# Revit family: QSC TSC80W-G2_R15
name_source: partatom
category: Communication Devices
revit_build: Autodesk Revit 2015 (Build: 20160512_0715(x64)
units: mm (PartAtom-declared; Revit-internal decimal feet)

## types (1)
- QSC TSC80W-G2_R15
    Brightness Full = 400 Nits
    Current Draw = 0.5
    Default Elevation = 0.0 mm
    Depth = 33.7 mm
    Description = In-Wall or Table Top Touch Screen Controller
    Enclosure Material = Steel, Paint Finish, Dark Gray, Matte
    Face Material = Glossy Black
    Heat Load = 17 typical
    Height = 87.5 mm
    Manufacturer = QSC
    Manufacturer URL = http://www.qsc.com
    Model = TSC-55W-G2
    OmniClass Number = 23-19 11 25
    Product Documentation Link = https://www.qsc.com
    Resolution Horizontal = 960
    Resolution Vertical = 540
    Screen = Metal Panel
    Screen Height = 68.0 mm
    Screen Width = 122.0 mm
    Temperature Max = 122F/ 50C
    Temperature Min = 32F/ 0C
    URL = https://www.qsc.com
    Voltage DC = 24 VDC or PoE 802.3af
    Weight Product = 0.39
    Width = 148.5 mm

## geometry (parser evidence)
native form markers: Blend x3, Sweep x8
no freeform markers — native parametric forms only
